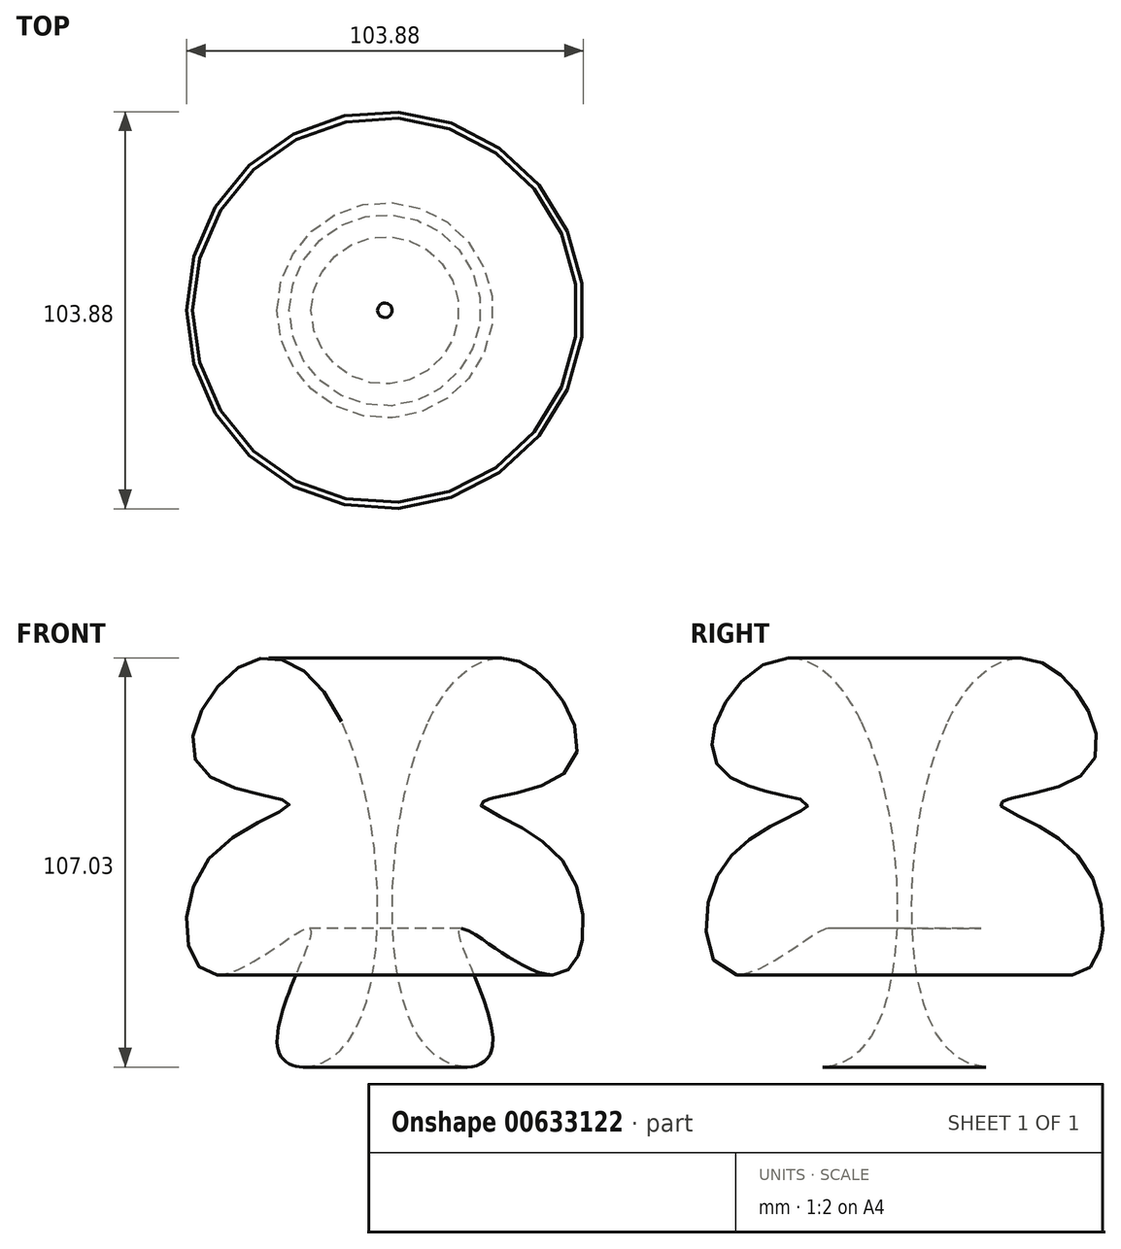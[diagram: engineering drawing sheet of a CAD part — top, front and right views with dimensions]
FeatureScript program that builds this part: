
annotation { "Feature Type Name" : "Feature", "Feature Type Description" : "" }
export const myFeature = defineFeature(function(context is Context, id is Id, definition is map)
    precondition{}
    {
        {
            var Q0;
            Q0=qCreatedBy(makeId("Top.planeOp"),FACE);
            var sketch = newSketch(context, id + "F0", { "sketchPlane" : qUnion([Q0])});
            skCircle(sketch, "E0", {"center": v(0, 0) * mm, "radius": 61.84 * mm});
            skSolve(sketch);
        }
        {
            var Q0;
            Q0=qCreatedBy(makeId("Front.planeOp"),FACE);
            var sketch = newSketch(context, id + "F1", { "sketchPlane" : qUnion([Q0])});
            skFitSpline(sketch, "E1", {"points": [v(-11.36, 34.28) * mm, v(-36.57, 49.36) * mm, v(-48.6, 22.44) * mm, v(-25.11, 12.89) * mm, v(-46.88, -2.77) * mm, v(-44.78, -31.98) * mm, v(-19.57, -19.95) * mm, v(-27.97, -51.46) * mm, v(-11.17, -51.27) * mm, v(-11.36, 34.28) * mm]});
            skSolve(sketch);
        }
        {
            var Q0;
            Q0=makeQuery(id+"F1.imprint","IMPRINT",FACE,{"disambiguationData":[TD([[makeQuery(id+"F1.imprint","IMPRINT",EDGE,{"derivedFrom":sQuery(id+"F1.wireOp",EDGE,"E1")}),1.0]])]});
            var Q1;
            Q1=sQuery(id+"F0.wireOp",EDGE,"E0");
            revolve(context, id + "F2", {"entities" : qUnion([Q0]), "axis" : qUnion([Q1]), "revolveType" : RevolveType.FULL});
        }
    });
